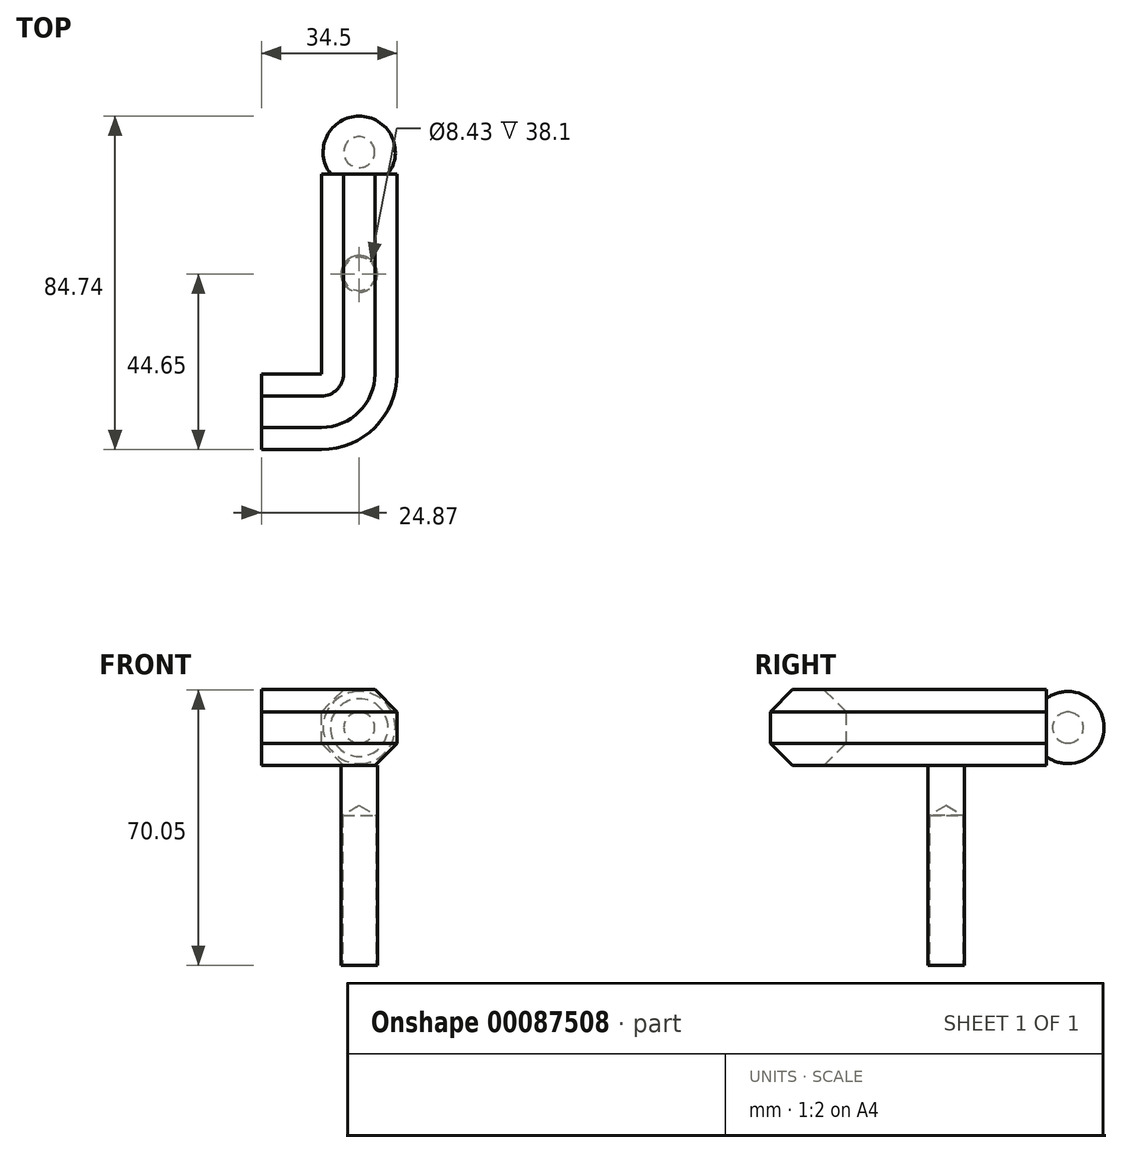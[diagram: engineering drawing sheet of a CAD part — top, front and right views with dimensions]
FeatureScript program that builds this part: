
annotation { "Feature Type Name" : "Feature", "Feature Type Description" : "" }
export const myFeature = defineFeature(function(context is Context, id is Id, definition is map)
    precondition{}
    {
        {
            var Q0;
            Q0=qCreatedBy(makeId("Top.planeOp"),FACE);
            var sketch = newSketch(context, id + "F0", { "sketchPlane" : qUnion([Q0])});
            skCircle(sketch, "E0", {"center": v(0, 0) * mm, "radius": 4.64 * mm});
            skSolve(sketch);
        }
        {
            var Q0;
            Q0=makeQuery(id+"F0.imprint","IMPRINT",FACE,{"disambiguationData":[TD([[makeQuery(id+"F0.imprint","IMPRINT",EDGE,{"derivedFrom":sQuery(id+"F0.wireOp",EDGE,"E0")}),1.0]])]});
            extrude(context, id + "F1", {"entities" : qUnion([Q0]), "depth" : 50.8 * mm});
        }
        {
            var Q0;
            Q0=sQuery(id+"F0.wireOp",VERTEX,"E0.center");
            var Q1;
            Q1=makeQuery(id+"F1.opExtrude","SWEPT_BODY",BODY,{"disambiguationData":[OSD([sQuery(id+"F0.wireOp",EDGE,"E0")])]});
            hole(context, id + "F2", {"style" : HoleStyle.SIMPLE, "endStyle" : HoleEndStyle.BLIND, "oppositeDirection" : true, "holeDiameter" : 8.43 * mm, "holeDepth" : 38.1 * mm, "locations" : qUnion([Q0]), "scope" : qUnion([Q1])});
        }
        {
            var Q0;
            Q0=qCreatedBy(makeId("Front.planeOp"),FACE);
            var sketch = newSketch(context, id + "F3", { "sketchPlane" : qUnion([Q0])});
            skCircle(sketch, "E1.cCircle", {"center": v(0, 60.43) * mm, "radius": 9.63 * mm, "construction": true});
            skLineSegment(sketch, "E1.0", {"start": v(-3.99, 50.8) * mm, "end": v(-9.63, 56.44) * mm});
            skLineSegment(sketch, "E1.1", {"start": v(-9.63, 56.44) * mm, "end": v(-9.63, 64.42) * mm});
            skLineSegment(sketch, "E1.2", {"start": v(-9.63, 64.42) * mm, "end": v(-3.99, 70.05) * mm});
            skLineSegment(sketch, "E1.3", {"start": v(-3.99, 70.05) * mm, "end": v(3.99, 70.05) * mm});
            skLineSegment(sketch, "E1.4", {"start": v(3.99, 70.05) * mm, "end": v(9.63, 64.42) * mm});
            skLineSegment(sketch, "E1.5", {"start": v(9.63, 64.42) * mm, "end": v(9.63, 56.44) * mm});
            skLineSegment(sketch, "E1.6", {"start": v(9.63, 56.44) * mm, "end": v(3.99, 50.8) * mm});
            skLineSegment(sketch, "E1.7", {"start": v(3.99, 50.8) * mm, "end": v(-3.99, 50.8) * mm});
            skPoint(sketch, "E1.0.midPoint", {"position": v(-6.8, 53.62) * mm});
            skLineSegment(sketch, "E2", {"start": v(0, 60.43) * mm, "end": v(0, 70.05) * mm});
            skSolve(sketch);
        }
        {
            var Q0;
            Q0=makeQuery(id+"F3.imprint","IMPRINT",FACE,{"disambiguationData":[TD([[makeQuery(id+"F3.imprint","IMPRINT",EDGE,{"derivedFrom":sQuery(id+"F3.wireOp",EDGE,"E1.0")}),-1.0]])]});
            extrude(context, id + "F4", {"entities" : qUnion([Q0]), "operationType" : NewBodyOperationType.ADD, "depth" : 25.4 * mm, "hasSecondDirection" : true, "secondDirectionOppositeDirection" : true, "secondDirectionDepth" : 25.4 * mm});
        }
        {
            var Q0;
            Q0=makeQuery(id+"F4.opExtrude","CAP_FACE",FACE,{"disambiguationData":[OSD([sQuery(id+"F3.wireOp",EDGE,"E1.0"),sQuery(id+"F3.wireOp",EDGE,"E1.1"),sQuery(id+"F3.wireOp",EDGE,"E1.2"),sQuery(id+"F3.wireOp",EDGE,"E1.3"),sQuery(id+"F3.wireOp",EDGE,"E1.4"),sQuery(id+"F3.wireOp",EDGE,"E1.5"),sQuery(id+"F3.wireOp",EDGE,"E1.6"),sQuery(id+"F3.wireOp",EDGE,"E1.7")])],"isStart":false});
            var Q1;
            Q1=makeQuery(id+"F4.opExtrude","CAP_EDGE",EDGE,{"disambiguationData":[OSD([sQuery(id+"F3.wireOp",EDGE,"E1.1")])],"isStart":false});
            revolve(context, id + "F5", {"operationType" : NewBodyOperationType.ADD, "entities" : qUnion([Q0]), "axis" : qUnion([Q1]), "revolveType" : RevolveType.ONE_DIRECTION, "oppositeDirection" : true, "angle" : 90 * degree});
        }
        {
            var Q0;
            Q0=makeQuery(id+"F4.opExtrude","CAP_FACE",FACE,{"disambiguationData":[OSD([sQuery(id+"F3.wireOp",EDGE,"E1.0"),sQuery(id+"F3.wireOp",EDGE,"E1.1"),sQuery(id+"F3.wireOp",EDGE,"E1.2"),sQuery(id+"F3.wireOp",EDGE,"E1.3"),sQuery(id+"F3.wireOp",EDGE,"E1.4"),sQuery(id+"F3.wireOp",EDGE,"E1.5"),sQuery(id+"F3.wireOp",EDGE,"E1.6"),sQuery(id+"F3.wireOp",EDGE,"E1.7")])],"isStart":true});
            var sketch = newSketch(context, id + "F6", { "sketchPlane" : qUnion([Q0])});
            skSolve(sketch);
        }
        {
            var Q0;
            Q0=qCreatedBy(makeId("Right.planeOp"),FACE);
            var sketch = newSketch(context, id + "F7", { "sketchPlane" : qUnion([Q0])});
            skCircle(sketch, "E3", {"center": v(30.92, 60.43) * mm, "radius": 9.17 * mm});
            skLineSegment(sketch, "E4", {"start": v(30.92, 60.43) * mm, "end": v(21.75, 60.43) * mm});
            skLineSegment(sketch, "E5", {"start": v(30.92, 69.6) * mm, "end": v(30.92, 51.26) * mm});
            skLineSegment(sketch, "E6", {"start": v(30.92, 60.43) * mm, "end": v(22.12, 63.01) * mm});
            skLineSegment(sketch, "E7", {"start": v(22.12, 63.01) * mm, "end": v(22.12, 57.84) * mm});
            skLineSegment(sketch, "E8", {"start": v(22.12, 57.84) * mm, "end": v(30.92, 60.43) * mm});
            skLineSegment(sketch, "E9", {"start": v(25.4, 62.05) * mm, "end": v(25.4, 58.8) * mm});
            skPoint(sketch, "E10", {"position": v(25.4, 53.1) * mm});
            skPoint(sketch, "E11", {"position": v(25.4, 67.75) * mm});
            skLineSegment(sketch, "E12", {"start": v(25.4, 67.75) * mm, "end": v(25.4, 62.05) * mm});
            skLineSegment(sketch, "E13", {"start": v(25.4, 58.8) * mm, "end": v(25.4, 53.1) * mm});
            skSolve(sketch);
        }
        {
            var Q0;
            {var subQ0=sQuery(id+"F7.wireOp",EDGE,"E5");var subQ1=sQuery(id+"F7.wireOp",EDGE,"E3");var subQ2=makeQuery(id+"F7.imprint","INTERSECT",VERTEX,{"disambiguationData":[OD(0.0)],"derivedFrom":[subQ1,subQ0]});Q0=makeQuery(id+"F7.imprint","IMPRINT",FACE,{"disambiguationData":[TD([[makeQuery(id+"F7.imprint","IMPRINT",EDGE,{"disambiguationData":[TD([[subQ2,1.0]])],"derivedFrom":subQ1}),1.0]])]});}
            var Q1;
            Q1=sQuery(id+"F7.wireOp",EDGE,"E5");
            revolve(context, id + "F8", {"operationType" : NewBodyOperationType.ADD, "entities" : qUnion([Q0]), "axis" : qUnion([Q1]), "revolveType" : RevolveType.FULL});
        }
        {
            var Q0;
            {var subQ0=sQuery(id+"F3.wireOp",EDGE,"E1.1");Q0=makeQuery(id+"F5.boolean.opBoolean","MERGE",FACE,{"derivedFrom":[makeQuery(id+"F4.opExtrude","SWEPT_FACE",FACE,{"disambiguationData":[OSD([subQ0])]}),makeQuery(id+"F5.opRevolve","CAP_FACE",FACE,{"disambiguationData":[OSD([sQuery(id+"F3.wireOp",EDGE,"E1.0"),subQ0,sQuery(id+"F3.wireOp",EDGE,"E1.2"),sQuery(id+"F3.wireOp",EDGE,"E1.3"),sQuery(id+"F3.wireOp",EDGE,"E1.4"),sQuery(id+"F3.wireOp",EDGE,"E1.5"),sQuery(id+"F3.wireOp",EDGE,"E1.6"),sQuery(id+"F3.wireOp",EDGE,"E1.7")])],"isStart":false})]});}
            var sketch = newSketch(context, id + "F9", { "sketchPlane" : qUnion([Q0])});
            skCircle(sketch, "E14.cCircle", {"center": v(35.03, 60.43) * mm, "radius": 9.63 * mm, "construction": true});
            skLineSegment(sketch, "E14.0", {"start": v(39.02, 50.8) * mm, "end": v(31.04, 50.8) * mm});
            skLineSegment(sketch, "E14.1", {"start": v(31.04, 50.8) * mm, "end": v(25.4, 56.44) * mm});
            skLineSegment(sketch, "E14.2", {"start": v(25.4, 56.44) * mm, "end": v(25.4, 64.42) * mm});
            skLineSegment(sketch, "E14.3", {"start": v(25.4, 64.42) * mm, "end": v(31.04, 70.05) * mm});
            skLineSegment(sketch, "E14.4", {"start": v(31.04, 70.05) * mm, "end": v(39.02, 70.05) * mm});
            skLineSegment(sketch, "E14.5", {"start": v(39.02, 70.05) * mm, "end": v(44.65, 64.42) * mm});
            skLineSegment(sketch, "E14.6", {"start": v(44.65, 64.42) * mm, "end": v(44.65, 56.44) * mm});
            skLineSegment(sketch, "E14.7", {"start": v(44.65, 56.44) * mm, "end": v(39.02, 50.8) * mm});
            skPoint(sketch, "E14.0.midPoint", {"position": v(35.03, 50.8) * mm});
            skSolve(sketch);
        }
        {
            var Q0;
            Q0=qSketchRegion(id+"F9",true);
            extrude(context, id + "F10", {"entities" : qUnion([Q0]), "operationType" : NewBodyOperationType.ADD, "depth" : 15.24 * mm});
        }
        {
            var Q0;
            Q0=qCreatedBy(makeId("Right.planeOp"),FACE);
            cPlane(context, id + "F11", {"entities" : qUnion([Q0]), "cplaneType" : CPlaneType.OFFSET, "offset" : 20.32 * mm, "oppositeDirection" : true, "width" : 152.4 * mm, "height" : 152.4 * mm});
        }
        {
            var Q0;
            Q0=qCreatedBy(id+"F11.planeOp",FACE);
            var sketch = newSketch(context, id + "F12", { "sketchPlane" : qUnion([Q0])});
            skCircle(sketch, "E15.cCircle", {"center": v(-35.03, 60.43) * mm, "radius": 15.46 * mm, "construction": true});
            skLineSegment(sketch, "E15.0", {"start": v(-41.43, 44.97) * mm, "end": v(-50.49, 54.02) * mm});
            skLineSegment(sketch, "E15.1", {"start": v(-50.49, 54.02) * mm, "end": v(-50.49, 66.83) * mm});
            skLineSegment(sketch, "E15.2", {"start": v(-50.49, 66.83) * mm, "end": v(-41.43, 75.89) * mm});
            skLineSegment(sketch, "E15.3", {"start": v(-41.43, 75.89) * mm, "end": v(-28.62, 75.89) * mm});
            skLineSegment(sketch, "E15.4", {"start": v(-28.62, 75.89) * mm, "end": v(-19.57, 66.83) * mm});
            skLineSegment(sketch, "E15.5", {"start": v(-19.57, 66.83) * mm, "end": v(-19.57, 54.02) * mm});
            skLineSegment(sketch, "E15.6", {"start": v(-19.57, 54.02) * mm, "end": v(-28.62, 44.97) * mm});
            skLineSegment(sketch, "E15.7", {"start": v(-28.62, 44.97) * mm, "end": v(-41.43, 44.97) * mm});
            skPoint(sketch, "E15.0.midPoint", {"position": v(-45.96, 49.5) * mm});
            skSolve(sketch);
        }
        {
            var Q0;
            Q0=qCreatedBy(makeId("Right.planeOp"),FACE);
            var sketch = newSketch(context, id + "F13", { "sketchPlane" : qUnion([Q0])});
            skCircle(sketch, "E16", {"center": v(30.92, 60.43) * mm, "radius": 3.93 * mm});
            skLineSegment(sketch, "E17", {"start": v(30.92, 64.36) * mm, "end": v(30.92, 60.43) * mm});
            skLineSegment(sketch, "E18", {"start": v(30.92, 60.43) * mm, "end": v(30.92, 56.5) * mm});
            skSolve(sketch);
        }
        {
            var Q0;
            {var subQ0=sQuery(id+"F13.wireOp",EDGE,"E17");Q0=makeQuery(id+"F13.imprint","IMPRINT",FACE,{"disambiguationData":[TD([[makeQuery(id+"F13.imprint","IMPRINT",EDGE,{"derivedFrom":subQ0}),1.0]])]});}
            var Q1;
            Q1=sQuery(id+"F13.wireOp",EDGE,"E17");
            revolve(context, id + "F14", {"operationType" : NewBodyOperationType.REMOVE, "entities" : qUnion([Q0]), "axis" : qUnion([Q1]), "revolveType" : RevolveType.FULL});
        }
    });
